# Revit family: P300329-009
name_source: partatom
category: Lighting Fixtures
revit_build: Autodesk Revit 2017 (Build: 20160225_1515(x64)
units: mm (PartAtom-declared; Revit-internal decimal feet)

## family parameters
Cut with Voids When Loaded = No
Host = Face
Light Source = No
OmniClass Number = 23.80.70.11.14.17
OmniClass Title = Direct/Indirect
Part Type = Normal
Room Calculation Point = No
Round Connector Dimension = Use Diameter
Shared = Yes

## types (1)
- P300329-009
    Apparent Load = 100 VA
    Assembly Code = D5020200
    Connector Description = Lighting Connector
    Default Elevation = 48 "
    Description = Merry Collection Three-Light Brushed Nickel and Etched Glass Transitional Style Bath Vanity Wall Light
    Features = Incorporate a clean, contemporary design with the Merry Collection 3-Light Etched Glass Brushed Nickel Transitional Bath Vanity Light. Light sources glow from within crisp etched glass shades for a generous elegant glow sure to transform any bath into a modern retreat. The rectangular backplate, curved arms, and round light bases are coated in a beautiful brushed nickel finish that perfectly blends transitional and modern character. For ideal illumination, use 3 medium base bulbs that are sold separately (100w max - LED/CFL/incandescent). The bath light is compatible with dimmable bulbs. The bath vanity light's contemporary design is ideal for any bathroom in modern and transitional style settings. It's time to breathe new life into the mundane every day with timeless and truly transformative lighting. Make your purchase today to begin your journey to a whole new lighting experience. Progress Lighting products are designed for exceptional quality, reliability, and functionality.
Application: Ideal for any bathroom.
Style: Perfect for modern and transitional style settings.
Finish: The rectangular backplate, curved arms, and round light bases are coated in a beautiful brushed nickel finish that perfectly blends transitional and modern character.
Materials: Constructed from steel to ensure a long product lifespan.
Glass: Light sources glow from within crisp etched glass shades for a generous elegant glow to transform any bath into a modern retreat.
Dimensions: For ideal illumination, use 3 medium base bulbs that are sold separately (100w max - LED/CFL/incandescent). Compatible with dimmable bulbs.
Dimensions: Measures 24-inch length by 8.25-inch height by 5.75-inch depth (installed).
Certifications: cULus damp location listed.
Pairs With: Pairs with Progress Lighting fixtures from the Tobin, Etched Glass Flush, and Dome Glass collections.
Warranty: Our 1-Year Limited Warranty guarantees your complete satisfaction with your purchase and includes professional after-sales customer service support. Make your purchase today to breathe new life into your lighting design!
    Glass = Paint - Hubbell - White Texture
    Housing Material = Paint - Hubbell - Metallic Silver Textured
    Lamp = LED/CFL/incandescent
    Load Classification = Lighting
    Manufacturer = Progress Lighting
    Model = P300329-009
    Power Factor = 1
    Product Documentation Link = https://hubbellcdn.com
    Product Link = https://www.hubbell.com
    URL = https://www.hubbell.com
    Voltage = 120 V
    Warranty = 1 year Warranty
    Wattage Comments = 100W
    Watts = 100 W

## geometry (parser evidence)
native form markers: Sweep x6
no freeform markers — native parametric forms only
